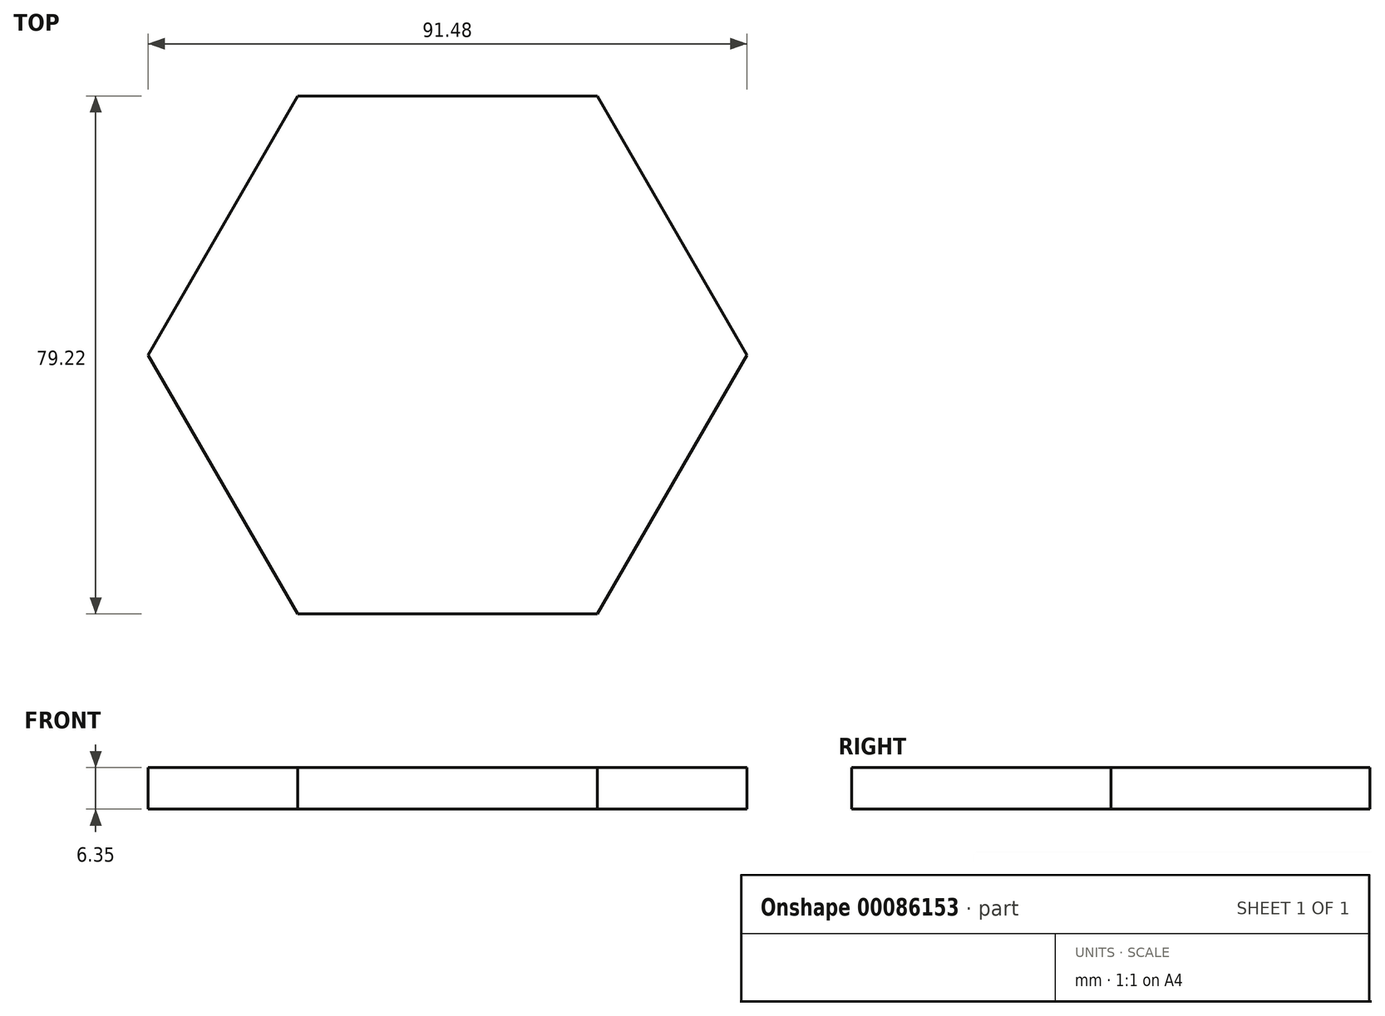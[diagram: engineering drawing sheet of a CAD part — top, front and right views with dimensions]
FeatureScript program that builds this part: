
annotation { "Feature Type Name" : "Feature", "Feature Type Description" : "" }
export const myFeature = defineFeature(function(context is Context, id is Id, definition is map)
    precondition{}
    {
        {
            var Q0;
            Q0=qCreatedBy(makeId("Top.planeOp"),FACE);
            var sketch = newSketch(context, id + "F0", { "sketchPlane" : qUnion([Q0])});
            skPoint(sketch, "E0", {"position": v(45.74, 0) * mm});
            skCircle(sketch, "E1.cCircle", {"center": v(0, 0) * mm, "radius": 45.74 * mm, "construction": true});
            skLineSegment(sketch, "E1.0", {"start": v(45.74, 0) * mm, "end": v(22.87, -39.61) * mm});
            skLineSegment(sketch, "E1.1", {"start": v(22.87, -39.61) * mm, "end": v(-22.87, -39.61) * mm});
            skLineSegment(sketch, "E1.2", {"start": v(-22.87, -39.61) * mm, "end": v(-45.74, 0) * mm});
            skLineSegment(sketch, "E1.3", {"start": v(-45.74, 0) * mm, "end": v(-22.87, 39.61) * mm});
            skLineSegment(sketch, "E1.4", {"start": v(-22.87, 39.61) * mm, "end": v(22.87, 39.61) * mm});
            skLineSegment(sketch, "E1.5", {"start": v(22.87, 39.61) * mm, "end": v(45.74, 0) * mm});
            skSolve(sketch);
        }
        {
            var Q0;
            Q0=makeQuery(id+"F0.imprint","IMPRINT",FACE,{"disambiguationData":[TD([[makeQuery(id+"F0.imprint","IMPRINT",EDGE,{"derivedFrom":sQuery(id+"F0.wireOp",EDGE,"E1.0")}),-1.0]])]});
            extrude(context, id + "F1", {"entities" : qUnion([Q0]), "depth" : 6.35 * mm});
        }
    });
